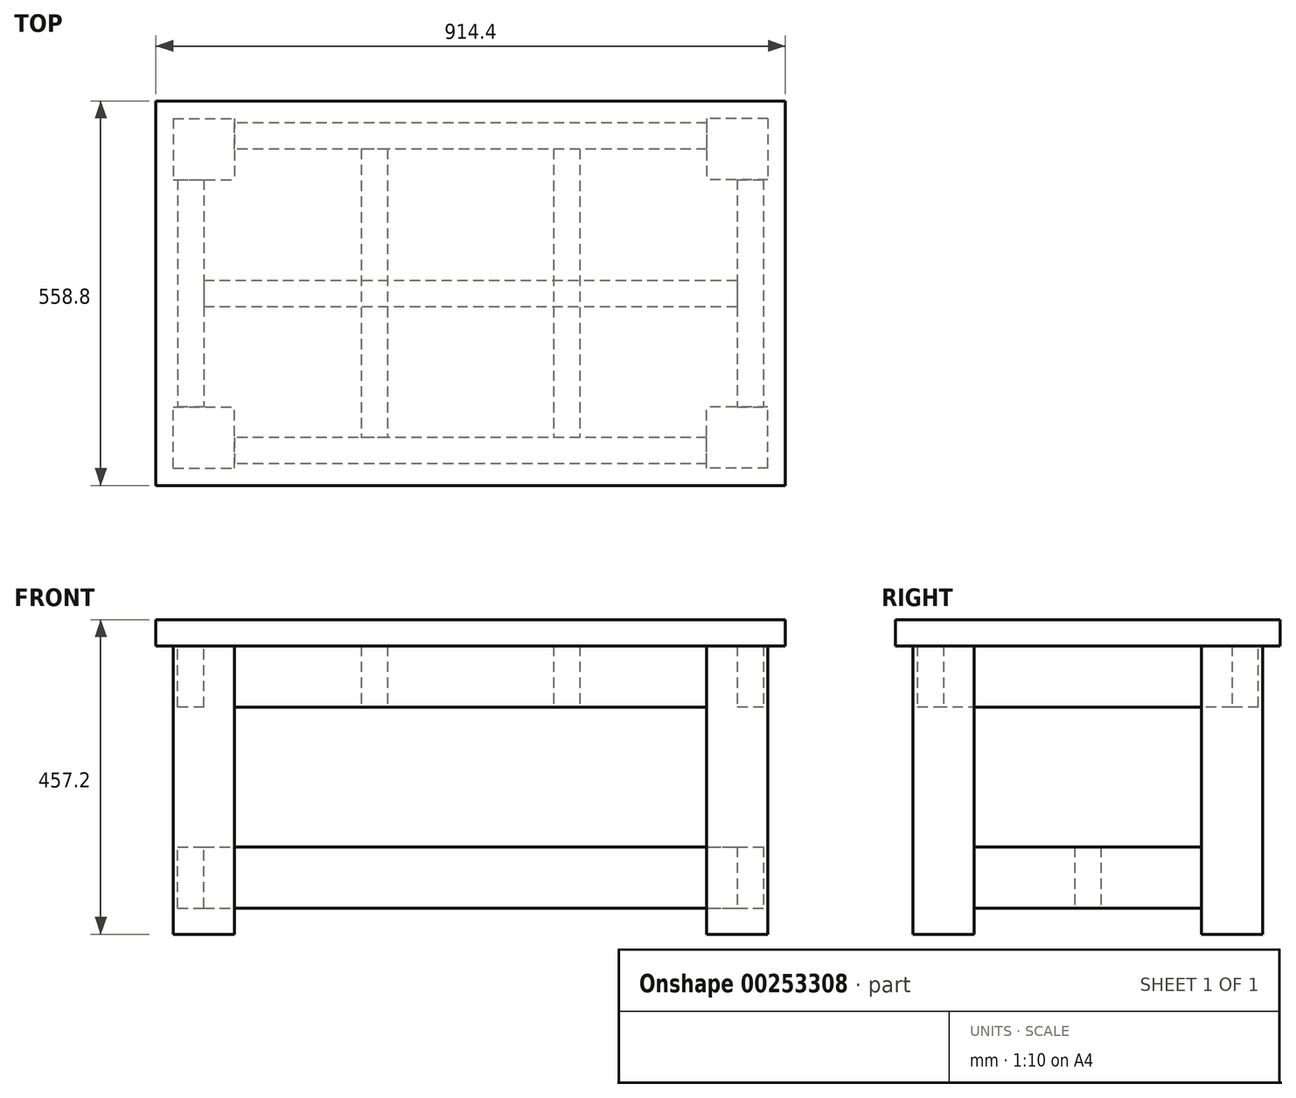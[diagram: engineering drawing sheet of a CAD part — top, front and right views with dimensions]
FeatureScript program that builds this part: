
annotation { "Feature Type Name" : "Feature", "Feature Type Description" : "" }
export const myFeature = defineFeature(function(context is Context, id is Id, definition is map)
    precondition{}
    {
        {
            var Q0;
            Q0=qCreatedBy(makeId("Top.planeOp"),FACE);
            var sketch = newSketch(context, id + "F0", { "sketchPlane" : qUnion([Q0])});
            skLineSegment(sketch, "E0.bottom", {"start": v(457.2, 279.4) * mm, "end": v(-457.2, 279.4) * mm});
            skLineSegment(sketch, "E0.top", {"start": v(457.2, -279.4) * mm, "end": v(-457.2, -279.4) * mm});
            skLineSegment(sketch, "E0.left", {"start": v(457.2, 279.4) * mm, "end": v(457.2, -279.4) * mm});
            skLineSegment(sketch, "E0.right", {"start": v(-457.2, 279.4) * mm, "end": v(-457.2, -279.4) * mm});
            skPoint(sketch, "E0.middle", {"position": v(0, 0) * mm});
            skSolve(sketch);
        }
        {
            var Q0;
            Q0=makeQuery(id+"F0.imprint","IMPRINT",FACE,{"disambiguationData":[TD([[makeQuery(id+"F0.imprint","IMPRINT",EDGE,{"derivedFrom":sQuery(id+"F0.wireOp",EDGE,"E0.bottom")}),1.0]])]});
            extrude(context, id + "F1", {"entities" : qUnion([Q0]), "depth" : 38.1 * mm});
        }
        {
            var Q0;
            Q0=makeQuery(id+"F1.opExtrude","CAP_FACE",FACE,{"disambiguationData":[OSD([sQuery(id+"F0.wireOp",EDGE,"E0.bottom"),sQuery(id+"F0.wireOp",EDGE,"E0.top"),sQuery(id+"F0.wireOp",EDGE,"E0.left"),sQuery(id+"F0.wireOp",EDGE,"E0.right")])],"isStart":true});
            var sketch = newSketch(context, id + "F2", { "sketchPlane" : qUnion([Q0])});
            skLineSegment(sketch, "E1.bottom", {"start": v(431.8, 254) * mm, "end": v(-431.8, 254) * mm, "construction": true});
            skLineSegment(sketch, "E1.top", {"start": v(431.8, -254) * mm, "end": v(-431.8, -254) * mm, "construction": true});
            skLineSegment(sketch, "E1.left", {"start": v(431.8, 254) * mm, "end": v(431.8, -254) * mm, "construction": true});
            skLineSegment(sketch, "E1.right", {"start": v(-431.8, 254) * mm, "end": v(-431.8, -254) * mm, "construction": true});
            skPoint(sketch, "E1.middle", {"position": v(0, 0) * mm});
            skLineSegment(sketch, "E2.bottom", {"start": v(-431.8, 254) * mm, "end": v(-342.9, 254) * mm});
            skLineSegment(sketch, "E2.top", {"start": v(-431.8, 165.1) * mm, "end": v(-342.9, 165.1) * mm});
            skLineSegment(sketch, "E2.left", {"start": v(-431.8, 254) * mm, "end": v(-431.8, 165.1) * mm});
            skLineSegment(sketch, "E2.right", {"start": v(-342.9, 254) * mm, "end": v(-342.9, 165.1) * mm});
            skLineSegment(sketch, "E3.bottom", {"start": v(431.8, 254) * mm, "end": v(342.9, 254) * mm});
            skLineSegment(sketch, "E3.top", {"start": v(431.8, 165.1) * mm, "end": v(342.9, 165.1) * mm});
            skLineSegment(sketch, "E3.left", {"start": v(431.8, 254) * mm, "end": v(431.8, 165.1) * mm});
            skLineSegment(sketch, "E3.right", {"start": v(342.9, 254) * mm, "end": v(342.9, 165.1) * mm});
            skLineSegment(sketch, "E4.bottom", {"start": v(431.8, -254) * mm, "end": v(342.9, -254) * mm});
            skLineSegment(sketch, "E4.top", {"start": v(431.8, -165.1) * mm, "end": v(342.9, -165.1) * mm});
            skLineSegment(sketch, "E4.left", {"start": v(431.8, -254) * mm, "end": v(431.8, -165.1) * mm});
            skLineSegment(sketch, "E4.right", {"start": v(342.9, -254) * mm, "end": v(342.9, -165.1) * mm});
            skLineSegment(sketch, "E5.bottom", {"start": v(-431.8, -254) * mm, "end": v(-342.9, -254) * mm});
            skLineSegment(sketch, "E5.top", {"start": v(-431.8, -165.1) * mm, "end": v(-342.9, -165.1) * mm});
            skLineSegment(sketch, "E5.left", {"start": v(-431.8, -254) * mm, "end": v(-431.8, -165.1) * mm});
            skLineSegment(sketch, "E5.right", {"start": v(-342.9, -254) * mm, "end": v(-342.9, -165.1) * mm});
            skSolve(sketch);
        }
        {
            var Q0;
            Q0 = qSketchRegion(id + "F2", true);
            extrude(context, id + "F3", {"entities" : qUnion([Q0]), "depth" : 419.1 * mm});
        }
        {
            var Q0;
            Q0=makeQuery(id+"F3.opExtrude","SWEPT_FACE",FACE,{"disambiguationData":[OSD([sQuery(id+"F2.wireOp",EDGE,"E3.top")])]});
            var sketch = newSketch(context, id + "F4", { "sketchPlane" : qUnion([Q0])});
            skLineSegment(sketch, "E6.0", {"start": v(-431.8, -419.1) * mm, "end": v(-431.8, 0) * mm, "construction": true});
            skLineSegment(sketch, "E6.1", {"start": v(-342.9, -419.1) * mm, "end": v(-342.9, 0) * mm, "construction": true});
            skLineSegment(sketch, "E6.2", {"start": v(-431.8, -419.1) * mm, "end": v(-342.9, -419.1) * mm, "construction": true});
            skLineSegment(sketch, "E7.bottom", {"start": v(-387.35, -292.1) * mm, "end": v(-425.45, -292.1) * mm});
            skLineSegment(sketch, "E7.top", {"start": v(-387.35, -381) * mm, "end": v(-425.45, -381) * mm});
            skLineSegment(sketch, "E7.left", {"start": v(-387.35, -292.1) * mm, "end": v(-387.35, -381) * mm});
            skLineSegment(sketch, "E7.right", {"start": v(-425.45, -292.1) * mm, "end": v(-425.45, -381) * mm});
            skPoint(sketch, "E7.middle", {"position": v(-406.4, -336.55) * mm});
            skLineSegment(sketch, "E8", {"start": v(-387.35, 0) * mm, "end": v(-387.35, -419.1) * mm, "construction": true});
            skLineSegment(sketch, "E9", {"start": v(0, 0) * mm, "end": v(0, -419.1) * mm, "construction": true});
            skLineSegment(sketch, "E10.MirrorCS", {"start": v(425.45, -292.1) * mm, "end": v(425.45, -381) * mm});
            skLineSegment(sketch, "E11.MirrorCS", {"start": v(387.35, -292.1) * mm, "end": v(387.35, -381) * mm});
            skLineSegment(sketch, "E12.MirrorCS", {"start": v(387.35, -381) * mm, "end": v(425.45, -381) * mm});
            skLineSegment(sketch, "E13.MirrorCS", {"start": v(387.35, -292.1) * mm, "end": v(425.45, -292.1) * mm});
            skPoint(sketch, "E14.MirrorP", {"position": v(406.4, -336.55) * mm});
            skSolve(sketch);
        }
        {
            var Q0;
            Q0 = qSketchRegion(id + "F4", true);
            extrude(context, id + "F5", {"entities" : qUnion([Q0]), "endBound" : BoundingType.UP_TO_NEXT, "depth" : 25.4 * mm});
        }
        {
            var Q0;
            Q0=makeQuery(id+"F3.opExtrude","SWEPT_FACE",FACE,{"disambiguationData":[OSD([sQuery(id+"F2.wireOp",EDGE,"E2.right")])]});
            var sketch = newSketch(context, id + "F6", { "sketchPlane" : qUnion([Q0])});
            skLineSegment(sketch, "E15.0", {"start": v(-165.1, -419.1) * mm, "end": v(-165.1, 0) * mm, "construction": true});
            skLineSegment(sketch, "E15.1", {"start": v(-254, -419.1) * mm, "end": v(-254, 0) * mm, "construction": true});
            skLineSegment(sketch, "E15.2", {"start": v(-254, -419.1) * mm, "end": v(-165.1, -419.1) * mm, "construction": true});
            skLineSegment(sketch, "E16.bottom", {"start": v(-190.5, -292.1) * mm, "end": v(-228.6, -292.1) * mm});
            skLineSegment(sketch, "E16.top", {"start": v(-190.5, -381) * mm, "end": v(-228.6, -381) * mm});
            skLineSegment(sketch, "E16.left", {"start": v(-190.5, -292.1) * mm, "end": v(-190.5, -381) * mm});
            skLineSegment(sketch, "E16.right", {"start": v(-228.6, -292.1) * mm, "end": v(-228.6, -381) * mm});
            skPoint(sketch, "E16.middle", {"position": v(-209.55, -336.55) * mm});
            skLineSegment(sketch, "E17", {"start": v(-209.55, -419.1) * mm, "end": v(-209.55, 0) * mm, "construction": true});
            skLineSegment(sketch, "E18", {"start": v(0, 0) * mm, "end": v(0, -419.1) * mm, "construction": true});
            skLineSegment(sketch, "E19.MirrorCS", {"start": v(190.5, -292.1) * mm, "end": v(228.6, -292.1) * mm});
            skLineSegment(sketch, "E20.MirrorCS", {"start": v(190.5, -381) * mm, "end": v(228.6, -381) * mm});
            skLineSegment(sketch, "E21.MirrorCS", {"start": v(228.6, -292.1) * mm, "end": v(228.6, -381) * mm});
            skLineSegment(sketch, "E22.MirrorCS", {"start": v(190.5, -292.1) * mm, "end": v(190.5, -381) * mm});
            skPoint(sketch, "E23.MirrorP", {"position": v(209.55, -336.55) * mm});
            skSolve(sketch);
        }
        {
            var Q0;
            Q0=makeQuery(id+"F5.opExtrude","SWEPT_FACE",FACE,{"disambiguationData":[OSD([sQuery(id+"F4.wireOp",EDGE,"E7.left")])]});
            var sketch = newSketch(context, id + "F7", { "sketchPlane" : qUnion([Q0])});
            skLineSegment(sketch, "E24.bottom", {"start": v(19.05, -292.1) * mm, "end": v(-19.05, -292.1) * mm});
            skLineSegment(sketch, "E24.top", {"start": v(19.05, -381) * mm, "end": v(-19.05, -381) * mm});
            skLineSegment(sketch, "E24.left", {"start": v(19.05, -292.1) * mm, "end": v(19.05, -381) * mm});
            skLineSegment(sketch, "E24.right", {"start": v(-19.05, -292.1) * mm, "end": v(-19.05, -381) * mm});
            skPoint(sketch, "E24.middle", {"position": v(0, -336.55) * mm});
            skSolve(sketch);
        }
        {
            var Q0;
            Q0 = qSketchRegion(id + "F7", true);
            extrude(context, id + "F8", {"entities" : qUnion([Q0]), "endBound" : BoundingType.UP_TO_NEXT, "depth" : 25.4 * mm});
        }
        {
            var Q0;
            Q0=makeQuery(id+"F3.opExtrude","SWEPT_FACE",FACE,{"disambiguationData":[OSD([sQuery(id+"F2.wireOp",EDGE,"E2.top")])]});
            var sketch = newSketch(context, id + "F9", { "sketchPlane" : qUnion([Q0])});
            skLineSegment(sketch, "E25.0", {"start": v(431.8, -419.1) * mm, "end": v(431.8, 0) * mm, "construction": true});
            skLineSegment(sketch, "E25.1", {"start": v(342.9, -419.1) * mm, "end": v(342.9, 0) * mm, "construction": true});
            skLineSegment(sketch, "E25.2", {"start": v(-457.2, 0) * mm, "end": v(457.2, 0) * mm, "construction": true});
            skLineSegment(sketch, "E26.bottom", {"start": v(425.45, 0) * mm, "end": v(387.35, 0) * mm});
            skLineSegment(sketch, "E26.top", {"start": v(425.45, -88.9) * mm, "end": v(387.35, -88.9) * mm});
            skLineSegment(sketch, "E26.left", {"start": v(425.45, 0) * mm, "end": v(425.45, -88.9) * mm});
            skLineSegment(sketch, "E26.right", {"start": v(387.35, 0) * mm, "end": v(387.35, -88.9) * mm});
            skPoint(sketch, "E26.middle", {"position": v(406.4, -44.45) * mm});
            skLineSegment(sketch, "E27", {"start": v(0, 0) * mm, "end": v(0, -419.1) * mm, "construction": true});
            skPoint(sketch, "E28.MirrorP", {"position": v(-406.4, -44.45) * mm});
            skLineSegment(sketch, "E29.MirrorCS", {"start": v(-425.45, 0) * mm, "end": v(-387.35, 0) * mm});
            skLineSegment(sketch, "E30.MirrorCS", {"start": v(-425.45, -88.9) * mm, "end": v(-387.35, -88.9) * mm});
            skLineSegment(sketch, "E31.MirrorCS", {"start": v(-425.45, 0) * mm, "end": v(-425.45, -88.9) * mm});
            skLineSegment(sketch, "E32.MirrorCS", {"start": v(-387.35, 0) * mm, "end": v(-387.35, -88.9) * mm});
            skSolve(sketch);
        }
        {
            var Q0;
            Q0=makeQuery(id+"F3.opExtrude","SWEPT_FACE",FACE,{"disambiguationData":[OSD([sQuery(id+"F2.wireOp",EDGE,"E2.right")])]});
            var sketch = newSketch(context, id + "F10", { "sketchPlane" : qUnion([Q0])});
            skLineSegment(sketch, "E33.0", {"start": v(-254, -419.1) * mm, "end": v(-254, 0) * mm, "construction": true});
            skLineSegment(sketch, "E33.1", {"start": v(279.4, 0) * mm, "end": v(-279.4, 0) * mm, "construction": true});
            skLineSegment(sketch, "E33.2", {"start": v(-165.1, 0) * mm, "end": v(-165.1, -88.9) * mm, "construction": true});
            skLineSegment(sketch, "E34.bottom", {"start": v(-209.55, 0) * mm, "end": v(-247.65, 0) * mm});
            skLineSegment(sketch, "E34.top", {"start": v(-209.55, -88.9) * mm, "end": v(-247.65, -88.9) * mm});
            skLineSegment(sketch, "E34.left", {"start": v(-209.55, 0) * mm, "end": v(-209.55, -88.9) * mm});
            skLineSegment(sketch, "E34.right", {"start": v(-247.65, 0) * mm, "end": v(-247.65, -88.9) * mm});
            skPoint(sketch, "E34.middle", {"position": v(-228.6, -44.45) * mm});
            skLineSegment(sketch, "E35", {"start": v(0, 0) * mm, "end": v(0, -419.1) * mm, "construction": true});
            skLineSegment(sketch, "E36.MirrorCS", {"start": v(209.55, 0) * mm, "end": v(247.65, 0) * mm});
            skLineSegment(sketch, "E37.MirrorCS", {"start": v(209.55, -88.9) * mm, "end": v(247.65, -88.9) * mm});
            skLineSegment(sketch, "E38.MirrorCS", {"start": v(209.55, 0) * mm, "end": v(209.55, -88.9) * mm});
            skLineSegment(sketch, "E39.MirrorCS", {"start": v(247.65, 0) * mm, "end": v(247.65, -88.9) * mm});
            skPoint(sketch, "E40.MirrorP", {"position": v(228.6, -44.45) * mm});
            skSolve(sketch);
        }
        {
            var Q0;
            Q0 = qSketchRegion(id + "F9", true);
            extrude(context, id + "F11", {"entities" : qUnion([Q0]), "endBound" : BoundingType.UP_TO_NEXT, "depth" : 25.4 * mm});
        }
        {
            var Q0;
            Q0 = qSketchRegion(id + "F10", true);
            extrude(context, id + "F12", {"entities" : qUnion([Q0]), "endBound" : BoundingType.UP_TO_NEXT, "depth" : 25.4 * mm});
        }
        {
            var Q0;
            Q0=makeQuery(id+"F12.opExtrude","SWEPT_FACE",FACE,{"disambiguationData":[OSD([sQuery(id+"F10.wireOp",EDGE,"E34.left")])]});
            var sketch = newSketch(context, id + "F13", { "sketchPlane" : qUnion([Q0])});
            skLineSegment(sketch, "E41.bottom", {"start": v(158.75, 0) * mm, "end": v(120.65, 0) * mm});
            skLineSegment(sketch, "E41.top", {"start": v(158.75, -88.9) * mm, "end": v(120.65, -88.9) * mm});
            skLineSegment(sketch, "E41.left", {"start": v(158.75, 0) * mm, "end": v(158.75, -88.9) * mm});
            skLineSegment(sketch, "E41.right", {"start": v(120.65, 0) * mm, "end": v(120.65, -88.9) * mm});
            skPoint(sketch, "E41.middle", {"position": v(139.7, -44.45) * mm});
            skLineSegment(sketch, "E42.bottom", {"start": v(-120.65, 0) * mm, "end": v(-158.75, 0) * mm});
            skLineSegment(sketch, "E42.top", {"start": v(-120.65, -88.9) * mm, "end": v(-158.75, -88.9) * mm});
            skLineSegment(sketch, "E42.left", {"start": v(-120.65, 0) * mm, "end": v(-120.65, -88.9) * mm});
            skLineSegment(sketch, "E42.right", {"start": v(-158.75, 0) * mm, "end": v(-158.75, -88.9) * mm});
            skPoint(sketch, "E42.middle", {"position": v(-139.7, -44.45) * mm});
            skLineSegment(sketch, "E43.0", {"start": v(-387.35, 0) * mm, "end": v(-387.35, -88.9) * mm, "construction": true});
            skLineSegment(sketch, "E43.1", {"start": v(387.35, 0) * mm, "end": v(387.35, -88.9) * mm, "construction": true});
            skLineSegment(sketch, "E44", {"start": v(-387.35, -44.45) * mm, "end": v(-158.75, -44.45) * mm, "construction": true});
            skLineSegment(sketch, "E45", {"start": v(-120.65, -44.45) * mm, "end": v(120.65, -44.45) * mm, "construction": true});
            skLineSegment(sketch, "E46", {"start": v(158.75, -44.45) * mm, "end": v(387.35, -44.45) * mm, "construction": true});
            skSolve(sketch);
        }
        {
            var Q0;
            Q0 = qSketchRegion(id + "F13", true);
            extrude(context, id + "F14", {"entities" : qUnion([Q0]), "endBound" : BoundingType.UP_TO_NEXT, "depth" : 25.4 * mm});
        }
    });
